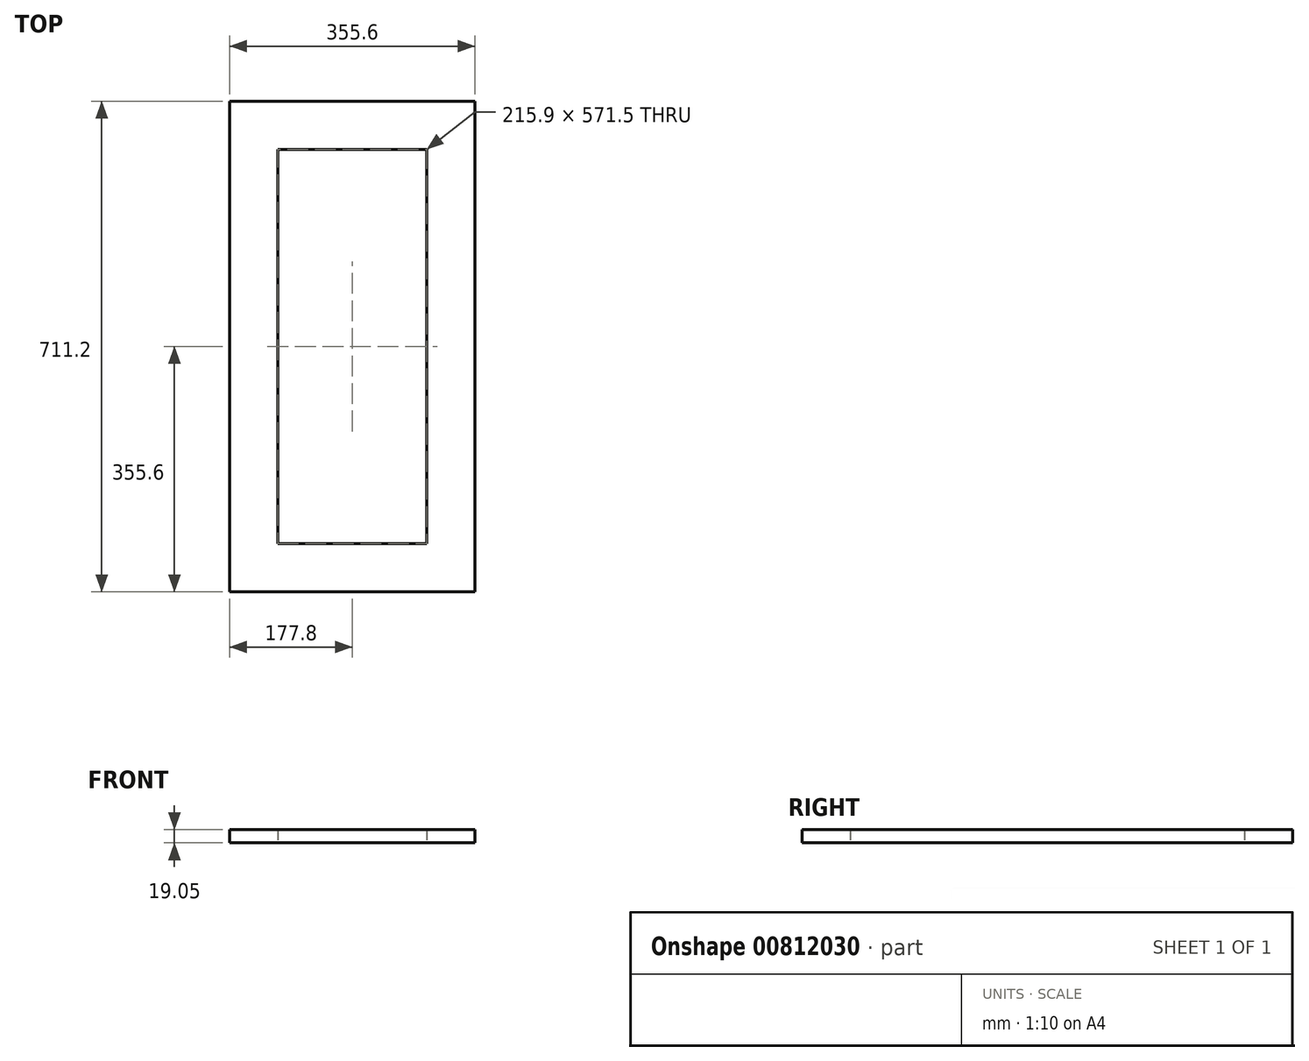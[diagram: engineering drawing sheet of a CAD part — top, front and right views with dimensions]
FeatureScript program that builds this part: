
annotation { "Feature Type Name" : "Feature", "Feature Type Description" : "" }
export const myFeature = defineFeature(function(context is Context, id is Id, definition is map)
    precondition{}
    {
        {
            var Q0;
            Q0=qCreatedBy(makeId("Top.planeOp"),FACE);
            var sketch = newSketch(context, id + "F0", { "sketchPlane" : qUnion([Q0])});
            skLineSegment(sketch, "E0.bottom", {"start": v(177.8, 355.6) * mm, "end": v(-177.8, 355.6) * mm});
            skLineSegment(sketch, "E0.top", {"start": v(177.8, -355.6) * mm, "end": v(-177.8, -355.6) * mm});
            skLineSegment(sketch, "E0.left", {"start": v(177.8, 355.6) * mm, "end": v(177.8, -355.6) * mm});
            skLineSegment(sketch, "E0.right", {"start": v(-177.8, 355.6) * mm, "end": v(-177.8, -355.6) * mm});
            skPoint(sketch, "E0.middle", {"position": v(0, 0) * mm});
            skLineSegment(sketch, "E1.bottom", {"start": v(107.95, 285.75) * mm, "end": v(-107.95, 285.75) * mm});
            skLineSegment(sketch, "E1.top", {"start": v(107.95, -285.75) * mm, "end": v(-107.95, -285.75) * mm});
            skLineSegment(sketch, "E1.left", {"start": v(107.95, 285.75) * mm, "end": v(107.95, -285.75) * mm});
            skLineSegment(sketch, "E1.right", {"start": v(-107.95, 285.75) * mm, "end": v(-107.95, -285.75) * mm});
            skSolve(sketch);
        }
        {
            var Q0;
            Q0=makeQuery(id+"F0.imprint","IMPRINT",FACE,{"disambiguationData":[TD([[makeQuery(id+"F0.imprint","IMPRINT",EDGE,{"derivedFrom":sQuery(id+"F0.wireOp",EDGE,"E0.bottom")}),1.0]])]});
            extrude(context, id + "F1", {"entities" : qUnion([Q0]), "depth" : 19.05 * mm, "offsetDistance" : 25.4 * mm});
        }
    });
